# Revit family: FantiniCosmi_BIM_CH120
name_source: partatom
category: Generic Models
units: mm (PartAtom-declared; Revit-internal decimal feet)

## family parameters
Always vertical = Yes
Can host rebar = No
Cut with Voids When Loaded = No
Part Type = Normal
Room Calculation Point = No
Round Connector Dimension = Use Diameter
Shared = No
Work Plane-Based = No

## types (1)
- Standard
    Body admissible temperature = - 10 ÷ 50 °C
    Catalog web link = https://www.fantinicosmi.it
    Default Elevation = 0 mm  [stored 0 ft]
    Description = Cronotermostato settimanale touchscreen, a batterie
    Differential = 0.3 ÷ 5 K
    Part Number = CH120
    Power supply = 2 batteries AA 1,5V
    Protection degree = IP20
    Pulse voltage = 4000V
    Software = A class
    Temperature range = 2 ÷ 40 °C
    Thermal gradient = 4K/h.
    Type of action = 1BU (micro disconnection)

note: [stored X ft] marks values corroborated as IEEE doubles in the binary element streams (Revit-internal decimal feet)

## geometry (parser evidence)
native form markers: Sweep x2
no freeform markers — native parametric forms only
